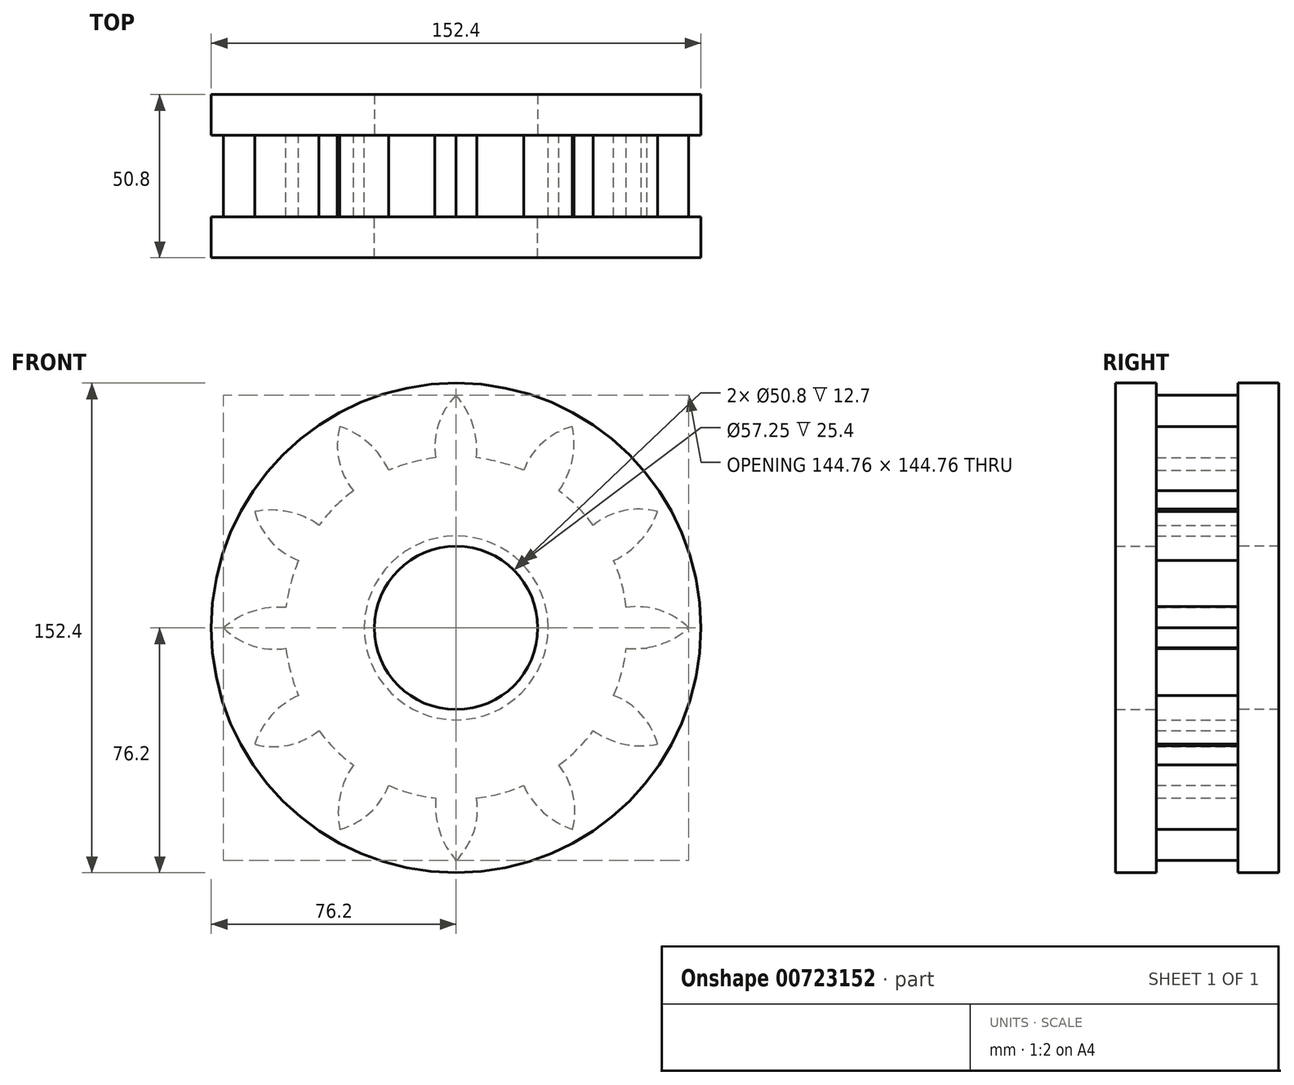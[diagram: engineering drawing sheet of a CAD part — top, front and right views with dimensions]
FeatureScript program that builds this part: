
annotation { "Feature Type Name" : "Feature", "Feature Type Description" : "" }
export const myFeature = defineFeature(function(context is Context, id is Id, definition is map)
    precondition{}
    {
        {
            var Q0;
            Q0=qCreatedBy(makeId("Front.planeOp"),FACE);
            var sketch = newSketch(context, id + "F0", { "sketchPlane" : qUnion([Q0])});
            skCircle(sketch, "E0.0", {"center": v(0, 0) * mm, "radius": 53.33 * mm});
            skCircle(sketch, "E1", {"center": v(0, 0) * mm, "radius": 28.62 * mm});
            skArc(sketch, "E2", {"start": v(72.38, 0) * mm, "mid": v(63.42, 5.5) * mm, "end": v(52.95, 6.35) * mm});
            skArc(sketch, "E3", {"start": v(52.95, -6.35) * mm, "mid": v(63.32, -5.18) * mm, "end": v(72.38, 0) * mm});
            skPoint(sketch, "E4.orphan", {"position": v(76.65, 6.35) * mm});
            skLineSegment(sketch, "E5.trimOffspring", {"start": v(59.34, 6.35) * mm, "end": v(59.83, 6.35) * mm});
            skArc(sketch, "E6.trimOffspring", {"start": v(59.34, 6.35) * mm, "mid": v(59.34, 6.38) * mm, "end": v(59.33, 6.42) * mm});
            skArc(sketch, "E7.trimOffspring", {"start": v(59.34, -6.35) * mm, "mid": v(59.35, -6.24) * mm, "end": v(59.36, -6.13) * mm});
            skLineSegment(sketch, "E8.trimOffspring", {"start": v(53.33, 0) * mm, "end": v(72.38, 0) * mm});
            skLineSegment(sketch, "E9.trimOffspring", {"start": v(52.95, -6.35) * mm, "end": v(59.34, -6.35) * mm});
            skPoint(sketch, "E10.start.orphan", {"position": v(-76.88, 0) * mm});
            skCircle(sketch, "E11", {"center": v(0, 0) * mm, "radius": 44.22 * mm});
            skArc(sketch, "E12.1.0", {"start": v(62.68, 36.2) * mm, "mid": v(52.18, 36.47) * mm, "end": v(42.68, 31.97) * mm});
            skArc(sketch, "E12.1.1", {"start": v(49.03, 20.98) * mm, "mid": v(57.42, 27.18) * mm, "end": v(62.68, 36.2) * mm});
            skArc(sketch, "E12.2.0", {"start": v(36.2, 62.68) * mm, "mid": v(26.96, 57.67) * mm, "end": v(20.98, 49.03) * mm});
            skArc(sketch, "E12.2.1", {"start": v(31.97, 42.68) * mm, "mid": v(36.14, 52.25) * mm, "end": v(36.2, 62.68) * mm});
            skArc(sketch, "E12.3.0", {"start": v(0, 72.38) * mm, "mid": v(-5.5, 63.42) * mm, "end": v(-6.35, 52.95) * mm});
            skArc(sketch, "E12.3.1", {"start": v(6.35, 52.95) * mm, "mid": v(5.18, 63.32) * mm, "end": v(0, 72.38) * mm});
            skArc(sketch, "E12.4.0", {"start": v(-36.2, 62.68) * mm, "mid": v(-36.47, 52.18) * mm, "end": v(-31.97, 42.68) * mm});
            skArc(sketch, "E12.4.1", {"start": v(-20.98, 49.03) * mm, "mid": v(-27.18, 57.42) * mm, "end": v(-36.2, 62.68) * mm});
            skArc(sketch, "E12.5.0", {"start": v(-62.68, 36.2) * mm, "mid": v(-57.67, 26.96) * mm, "end": v(-49.03, 20.98) * mm});
            skArc(sketch, "E12.5.1", {"start": v(-42.68, 31.97) * mm, "mid": v(-52.25, 36.14) * mm, "end": v(-62.68, 36.2) * mm});
            skArc(sketch, "E12.6.0", {"start": v(-72.38, 0) * mm, "mid": v(-63.42, -5.5) * mm, "end": v(-52.95, -6.35) * mm});
            skArc(sketch, "E12.6.1", {"start": v(-52.95, 6.35) * mm, "mid": v(-63.32, 5.18) * mm, "end": v(-72.38, 0) * mm});
            skArc(sketch, "E12.7.0", {"start": v(-62.68, -36.2) * mm, "mid": v(-52.18, -36.47) * mm, "end": v(-42.68, -31.97) * mm});
            skArc(sketch, "E12.7.1", {"start": v(-49.03, -20.98) * mm, "mid": v(-57.42, -27.18) * mm, "end": v(-62.68, -36.2) * mm});
            skArc(sketch, "E12.8.0", {"start": v(-36.2, -62.68) * mm, "mid": v(-26.96, -57.67) * mm, "end": v(-20.98, -49.03) * mm});
            skArc(sketch, "E12.8.1", {"start": v(-31.97, -42.68) * mm, "mid": v(-36.14, -52.25) * mm, "end": v(-36.2, -62.68) * mm});
            skArc(sketch, "E12.9.0", {"start": v(0, -72.38) * mm, "mid": v(5.5, -63.42) * mm, "end": v(6.35, -52.95) * mm});
            skArc(sketch, "E12.9.1", {"start": v(-6.35, -52.95) * mm, "mid": v(-5.18, -63.32) * mm, "end": v(0, -72.38) * mm});
            skArc(sketch, "E13.1.10.0", {"start": v(36.2, -62.68) * mm, "mid": v(36.47, -52.18) * mm, "end": v(31.97, -42.68) * mm});
            skArc(sketch, "E13.4.10.0", {"start": v(20.98, -49.03) * mm, "mid": v(27.18, -57.42) * mm, "end": v(36.2, -62.68) * mm});
            skArc(sketch, "E13.1.11.0", {"start": v(62.68, -36.2) * mm, "mid": v(57.67, -26.96) * mm, "end": v(49.03, -20.98) * mm});
            skArc(sketch, "E13.4.11.0", {"start": v(42.68, -31.97) * mm, "mid": v(52.25, -36.14) * mm, "end": v(62.68, -36.2) * mm});
            skSolve(sketch);
        }
        {
            var Q0;
            Q0 = qSketchRegion(id + "F0", true);
            var Q1;
            Q1=makeQuery(id+"F0.imprint","IMPRINT",FACE,{"disambiguationData":[TD([[makeQuery(id+"F0.imprint","IMPRINT",EDGE,{"derivedFrom":sQuery(id+"F0.wireOp",EDGE,"E1")}),-1.0]])]});
            extrude(context, id + "F1", {"entities" : qUnion([Q0, Q1]), "endBound" : BoundingType.SYMMETRIC, "depth" : 25.4 * mm, "offsetDistance" : 25.4 * mm});
        }
        {
            var Q0;
            Q0=makeQuery(id+"F1.opExtrude","CAP_FACE",FACE,{"disambiguationData":[OSD([sQuery(id+"F0.wireOp",EDGE,"E0.0"),sQuery(id+"F0.wireOp",EDGE,"E1"),sQuery(id+"F0.wireOp",EDGE,"E2"),sQuery(id+"F0.wireOp",EDGE,"E3"),sQuery(id+"F0.wireOp",EDGE,"E7.trimOffspring"),sQuery(id+"F0.wireOp",EDGE,"E9.trimOffspring"),sQuery(id+"F0.wireOp",EDGE,"E12.1.0"),sQuery(id+"F0.wireOp",EDGE,"E12.1.1"),sQuery(id+"F0.wireOp",EDGE,"E12.2.0"),sQuery(id+"F0.wireOp",EDGE,"E12.2.1"),sQuery(id+"F0.wireOp",EDGE,"E12.3.0"),sQuery(id+"F0.wireOp",EDGE,"E12.3.1"),sQuery(id+"F0.wireOp",EDGE,"E12.4.0"),sQuery(id+"F0.wireOp",EDGE,"E12.4.1"),sQuery(id+"F0.wireOp",EDGE,"E12.5.0"),sQuery(id+"F0.wireOp",EDGE,"E12.5.1"),sQuery(id+"F0.wireOp",EDGE,"E12.6.0"),sQuery(id+"F0.wireOp",EDGE,"E12.6.1"),sQuery(id+"F0.wireOp",EDGE,"E12.7.0"),sQuery(id+"F0.wireOp",EDGE,"E12.7.1"),sQuery(id+"F0.wireOp",EDGE,"E12.8.0"),sQuery(id+"F0.wireOp",EDGE,"E12.8.1"),sQuery(id+"F0.wireOp",EDGE,"E12.9.0"),sQuery(id+"F0.wireOp",EDGE,"E12.9.1"),sQuery(id+"F0.wireOp",EDGE,"E13.1.10.0"),sQuery(id+"F0.wireOp",EDGE,"E13.4.10.0"),sQuery(id+"F0.wireOp",EDGE,"E13.1.11.0"),sQuery(id+"F0.wireOp",EDGE,"E13.4.11.0")])],"isStart":false});
            var sketch = newSketch(context, id + "F2", { "sketchPlane" : qUnion([Q0])});
            skCircle(sketch, "E14", {"center": v(0, 0) * mm, "radius": 76.2 * mm});
            skCircle(sketch, "E15", {"center": v(0, 0) * mm, "radius": 25.4 * mm});
            skSolve(sketch);
        }
        {
            var Q0;
            Q0 = qSketchRegion(id + "F2", true);
            extrude(context, id + "F3", {"entities" : qUnion([Q0]), "operationType" : NewBodyOperationType.ADD, "depth" : 12.7 * mm, "offsetDistance" : 25.4 * mm});
        }
        {
            var Q0;
            Q0=makeQuery(id+"F1.opExtrude","CAP_FACE",FACE,{"disambiguationData":[OSD([sQuery(id+"F0.wireOp",EDGE,"E0.0"),sQuery(id+"F0.wireOp",EDGE,"E1"),sQuery(id+"F0.wireOp",EDGE,"E2"),sQuery(id+"F0.wireOp",EDGE,"E3"),sQuery(id+"F0.wireOp",EDGE,"E7.trimOffspring"),sQuery(id+"F0.wireOp",EDGE,"E9.trimOffspring"),sQuery(id+"F0.wireOp",EDGE,"E12.1.0"),sQuery(id+"F0.wireOp",EDGE,"E12.1.1"),sQuery(id+"F0.wireOp",EDGE,"E12.2.0"),sQuery(id+"F0.wireOp",EDGE,"E12.2.1"),sQuery(id+"F0.wireOp",EDGE,"E12.3.0"),sQuery(id+"F0.wireOp",EDGE,"E12.3.1"),sQuery(id+"F0.wireOp",EDGE,"E12.4.0"),sQuery(id+"F0.wireOp",EDGE,"E12.4.1"),sQuery(id+"F0.wireOp",EDGE,"E12.5.0"),sQuery(id+"F0.wireOp",EDGE,"E12.5.1"),sQuery(id+"F0.wireOp",EDGE,"E12.6.0"),sQuery(id+"F0.wireOp",EDGE,"E12.6.1"),sQuery(id+"F0.wireOp",EDGE,"E12.7.0"),sQuery(id+"F0.wireOp",EDGE,"E12.7.1"),sQuery(id+"F0.wireOp",EDGE,"E12.8.0"),sQuery(id+"F0.wireOp",EDGE,"E12.8.1"),sQuery(id+"F0.wireOp",EDGE,"E12.9.0"),sQuery(id+"F0.wireOp",EDGE,"E12.9.1"),sQuery(id+"F0.wireOp",EDGE,"E13.1.10.0"),sQuery(id+"F0.wireOp",EDGE,"E13.4.10.0"),sQuery(id+"F0.wireOp",EDGE,"E13.1.11.0"),sQuery(id+"F0.wireOp",EDGE,"E13.4.11.0")])],"isStart":true});
            var sketch = newSketch(context, id + "F4", { "sketchPlane" : qUnion([Q0])});
            skCircle(sketch, "E16", {"center": v(0, 0) * mm, "radius": 76.2 * mm});
            skCircle(sketch, "E17", {"center": v(0, 0) * mm, "radius": 25.4 * mm});
            skSolve(sketch);
        }
        {
            var Q0;
            Q0 = qSketchRegion(id + "F4", true);
            extrude(context, id + "F5", {"entities" : qUnion([Q0]), "operationType" : NewBodyOperationType.ADD, "depth" : 12.7 * mm, "offsetDistance" : 25.4 * mm});
        }
    });
